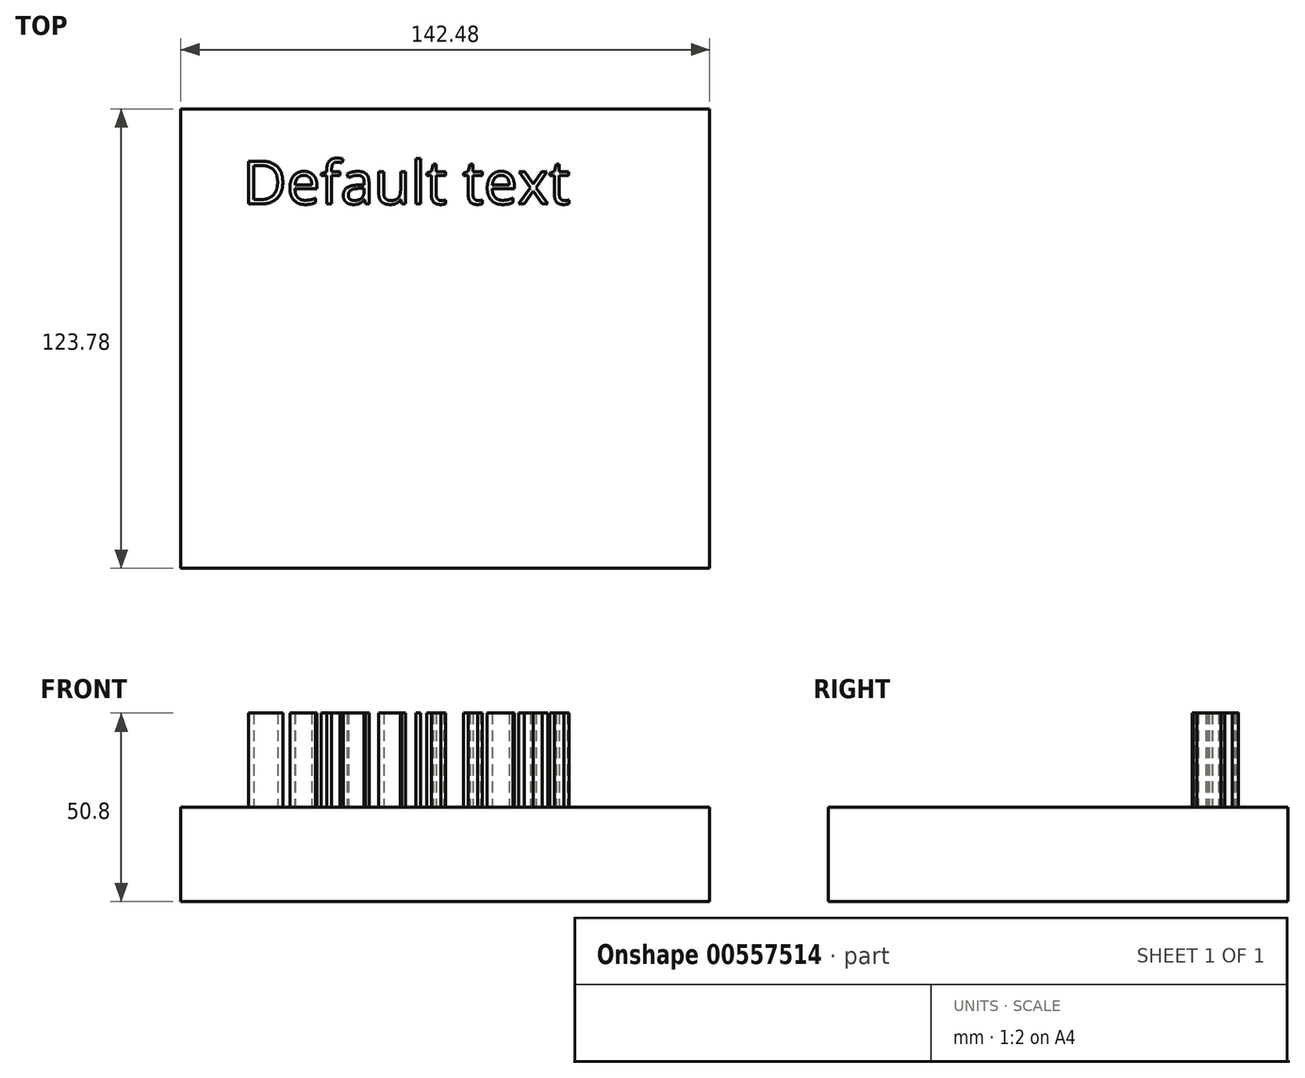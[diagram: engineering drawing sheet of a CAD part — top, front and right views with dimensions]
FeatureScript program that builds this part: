
annotation { "Feature Type Name" : "Feature", "Feature Type Description" : "" }
export const myFeature = defineFeature(function(context is Context, id is Id, definition is map)
    precondition{}
    {
        {
            var Q0;
            Q0=qCreatedBy(makeId("Top.planeOp"),FACE);
            var sketch = newSketch(context, id + "F0", { "sketchPlane" : qUnion([Q0])});
            skLineSegment(sketch, "E0.bottom", {"start": v(-72.97, 70.74) * mm, "end": v(69.51, 70.74) * mm});
            skLineSegment(sketch, "E0.top", {"start": v(-72.97, -53.04) * mm, "end": v(69.51, -53.04) * mm});
            skLineSegment(sketch, "E0.left", {"start": v(-72.97, 70.74) * mm, "end": v(-72.97, -53.04) * mm});
            skLineSegment(sketch, "E0.right", {"start": v(69.51, 70.74) * mm, "end": v(69.51, -53.04) * mm});
            skSolve(sketch);
        }
        {
            var Q0;
            Q0=makeQuery(id+"F0.imprint","IMPRINT",FACE,{"disambiguationData":[TD([[makeQuery(id+"F0.imprint","IMPRINT",EDGE,{"derivedFrom":sQuery(id+"F0.wireOp",EDGE,"E0.bottom")}),-1.0]])]});
            extrude(context, id + "F1", {"entities" : qUnion([Q0]), "depth" : 25.4 * mm, "offsetDistance" : 25.4 * mm});
        }
        {
            var Q0;
            Q0=makeQuery(id+"F1.opExtrude","CAP_FACE",FACE,{"disambiguationData":[OSD([sQuery(id+"F0.wireOp",EDGE,"E0.bottom"),sQuery(id+"F0.wireOp",EDGE,"E0.top"),sQuery(id+"F0.wireOp",EDGE,"E0.left"),sQuery(id+"F0.wireOp",EDGE,"E0.right")])],"isStart":false});
            var sketch = newSketch(context, id + "F2", { "sketchPlane" : qUnion([Q0])});
            skText(sketch, "E1", { "text": "Default text", "fontName": "OpenSans-Regular.ttf"});
            const initialGuessF2  = {"E1": [-0.05627, 0.04512, 1, 0, 0.01164]};
            skSetInitialGuess(sketch, initialGuessF2);
            skSolve(sketch);
        }
        {
            var Q0;
            Q0 = qSketchRegion(id + "F2", true);
            extrude(context, id + "F3", {"entities" : qUnion([Q0]), "operationType" : NewBodyOperationType.ADD, "depth" : 25.4 * mm, "offsetDistance" : 25.4 * mm});
        }
    });
